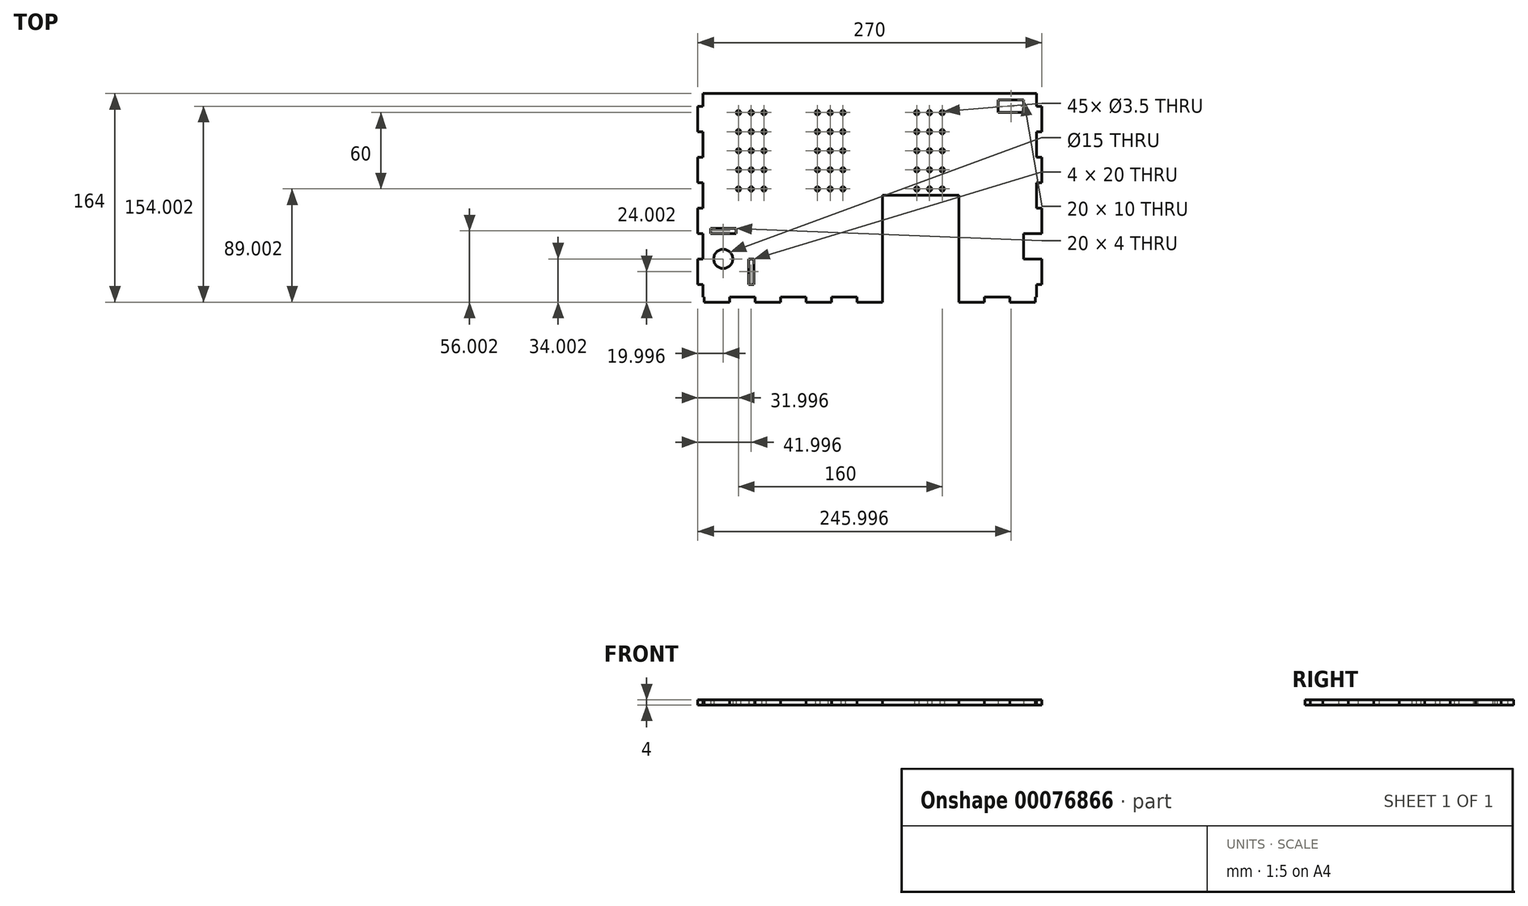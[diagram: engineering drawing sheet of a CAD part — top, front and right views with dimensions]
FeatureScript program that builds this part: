
annotation { "Feature Type Name" : "Feature", "Feature Type Description" : "" }
export const myFeature = defineFeature(function(context is Context, id is Id, definition is map)
    precondition{}
    {
        {
            var Q0;
            Q0=qCreatedBy(makeId("Top.planeOp"),FACE);
            var sketch = newSketch(context, id + "F0", { "sketchPlane" : qUnion([Q0])});
            skLineSegment(sketch, "E0.bottom", {"start": v(-142.44, 35.87) * mm, "end": v(119.56, 35.87) * mm, "construction": true});
            skLineSegment(sketch, "E0.top", {"start": v(-142.44, -124.13) * mm, "end": v(118.25, -124.13) * mm, "construction": true});
            skLineSegment(sketch, "E0.left", {"start": v(-142.44, 35.87) * mm, "end": v(-142.44, -124.13) * mm, "construction": true});
            skLineSegment(sketch, "E1", {"start": v(-11.44, 145.86) * mm, "end": v(-11.44, -140.18) * mm, "construction": true});
            skLineSegment(sketch, "E2.top", {"start": v(-1.44, -128.13) * mm, "end": v(-21.44, -128.13) * mm});
            skLineSegment(sketch, "E2.left", {"start": v(-1.44, -124.13) * mm, "end": v(-1.44, -128.13) * mm});
            skLineSegment(sketch, "E2.right", {"start": v(-21.44, -124.13) * mm, "end": v(-21.44, -128.13) * mm});
            skLineSegment(sketch, "E3.2.0.0", {"start": v(58.56, -124.13) * mm, "end": v(58.56, -128.13) * mm});
            skLineSegment(sketch, "E3.2.0.1", {"start": v(78.56, -128.13) * mm, "end": v(58.56, -128.13) * mm});
            skLineSegment(sketch, "E3.2.0.2", {"start": v(78.56, -124.13) * mm, "end": v(78.56, -128.13) * mm});
            skLineSegment(sketch, "E3.3.0.0", {"start": v(98.56, -124.13) * mm, "end": v(98.56, -128.13) * mm});
            skLineSegment(sketch, "E3.3.0.1", {"start": v(118.56, -128.13) * mm, "end": v(98.56, -128.13) * mm});
            skLineSegment(sketch, "E3.3.0.2", {"start": v(118.56, -124.13) * mm, "end": v(118.56, -128.13) * mm});
            skLineSegment(sketch, "E3.direction1", {"start": v(-21.44, -128.13) * mm, "end": v(18.56, -128.13) * mm, "construction": true});
            skLineSegment(sketch, "E4.1.0.0", {"start": v(-61.44, -124.13) * mm, "end": v(-61.44, -128.13) * mm});
            skLineSegment(sketch, "E4.1.0.1", {"start": v(-41.44, -128.13) * mm, "end": v(-61.44, -128.13) * mm});
            skLineSegment(sketch, "E4.1.0.2", {"start": v(-41.44, -124.13) * mm, "end": v(-41.44, -128.13) * mm});
            skLineSegment(sketch, "E4.2.0.0", {"start": v(-101.44, -124.13) * mm, "end": v(-101.44, -128.13) * mm});
            skLineSegment(sketch, "E4.2.0.1", {"start": v(-81.44, -128.13) * mm, "end": v(-101.44, -128.13) * mm});
            skLineSegment(sketch, "E4.2.0.2", {"start": v(-81.44, -124.13) * mm, "end": v(-81.44, -128.13) * mm});
            skLineSegment(sketch, "E4.direction1", {"start": v(-21.44, -128.13) * mm, "end": v(-61.44, -128.13) * mm, "construction": true});
            skLineSegment(sketch, "E5", {"start": v(78.56, -124.13) * mm, "end": v(98.56, -124.13) * mm});
            skLineSegment(sketch, "E6", {"start": v(-21.44, -124.13) * mm, "end": v(-41.44, -124.13) * mm});
            skLineSegment(sketch, "E7.0.3.0", {"start": v(-141.44, -124.13) * mm, "end": v(-141.44, -128.13) * mm});
            skLineSegment(sketch, "E7.3.3.0", {"start": v(-121.44, -128.13) * mm, "end": v(-141.44, -128.13) * mm});
            skLineSegment(sketch, "E7.6.3.0", {"start": v(-121.44, -124.13) * mm, "end": v(-121.44, -128.13) * mm});
            skLineSegment(sketch, "E8", {"start": v(-61.44, -124.13) * mm, "end": v(-81.44, -124.13) * mm});
            skLineSegment(sketch, "E9", {"start": v(-101.44, -124.13) * mm, "end": v(-121.44, -124.13) * mm});
            skLineSegment(sketch, "E10.top", {"start": v(58.56, -44.13) * mm, "end": v(-1.44, -44.13) * mm});
            skLineSegment(sketch, "E10.left", {"start": v(58.56, -124.13) * mm, "end": v(58.56, -44.13) * mm});
            skLineSegment(sketch, "E10.right", {"start": v(-1.44, -124.13) * mm, "end": v(-1.44, -44.13) * mm});
            skLineSegment(sketch, "E11.bottom", {"start": v(-142.44, -114.13) * mm, "end": v(-146.44, -114.13) * mm});
            skLineSegment(sketch, "E11.top", {"start": v(-142.44, -94.13) * mm, "end": v(-146.44, -94.13) * mm});
            skLineSegment(sketch, "E11.right", {"start": v(-146.44, -114.13) * mm, "end": v(-146.44, -94.13) * mm});
            skLineSegment(sketch, "E12", {"start": v(-142.44, -124.13) * mm, "end": v(-142.44, -114.13) * mm});
            skLineSegment(sketch, "E13.0.1.0", {"start": v(-142.44, -54.13) * mm, "end": v(-146.44, -54.13) * mm});
            skLineSegment(sketch, "E13.0.1.1", {"start": v(-146.44, -74.13) * mm, "end": v(-146.44, -54.13) * mm});
            skLineSegment(sketch, "E13.0.1.2", {"start": v(-142.44, -74.13) * mm, "end": v(-146.44, -74.13) * mm});
            skLineSegment(sketch, "E13.0.2.0", {"start": v(-142.44, -14.13) * mm, "end": v(-146.44, -14.13) * mm});
            skLineSegment(sketch, "E13.0.2.1", {"start": v(-146.44, -34.13) * mm, "end": v(-146.44, -14.13) * mm});
            skLineSegment(sketch, "E13.0.2.2", {"start": v(-142.44, -34.13) * mm, "end": v(-146.44, -34.13) * mm});
            skLineSegment(sketch, "E13.0.3.0", {"start": v(-142.44, 25.87) * mm, "end": v(-146.44, 25.87) * mm});
            skLineSegment(sketch, "E13.0.3.1", {"start": v(-146.44, 5.87) * mm, "end": v(-146.44, 25.87) * mm});
            skLineSegment(sketch, "E13.0.3.2", {"start": v(-142.44, 5.87) * mm, "end": v(-146.44, 5.87) * mm});
            skLineSegment(sketch, "E13.direction1", {"start": v(-146.44, -94.13) * mm, "end": v(-120.62, -94.13) * mm, "construction": true});
            skLineSegment(sketch, "E13.direction2", {"start": v(-146.44, -94.13) * mm, "end": v(-146.44, -54.13) * mm, "construction": true});
            skLineSegment(sketch, "E14", {"start": v(-142.44, -94.13) * mm, "end": v(-142.44, -74.13) * mm});
            skLineSegment(sketch, "E15", {"start": v(-142.44, -54.13) * mm, "end": v(-142.44, -34.13) * mm});
            skLineSegment(sketch, "E16", {"start": v(-142.44, -14.13) * mm, "end": v(-142.44, 5.87) * mm});
            skLineSegment(sketch, "E17", {"start": v(-142.44, 25.87) * mm, "end": v(-142.44, 35.87) * mm});
            skLineSegment(sketch, "E18", {"start": v(-142.44, 35.87) * mm, "end": v(119.56, 35.87) * mm});
            skLineSegment(sketch, "E19.MirrorCS", {"start": v(119.56, -94.13) * mm, "end": v(123.56, -94.13) * mm});
            skLineSegment(sketch, "E20.MirrorCS", {"start": v(119.56, -54.13) * mm, "end": v(123.56, -54.13) * mm});
            skLineSegment(sketch, "E21.MirrorCS", {"start": v(119.56, -34.13) * mm, "end": v(123.56, -34.13) * mm});
            skLineSegment(sketch, "E22.MirrorCS", {"start": v(119.56, 25.87) * mm, "end": v(119.56, 35.87) * mm});
            skLineSegment(sketch, "E23.MirrorCS", {"start": v(119.56, -74.13) * mm, "end": v(123.56, -74.13) * mm});
            skLineSegment(sketch, "E24.MirrorCS", {"start": v(119.56, -14.13) * mm, "end": v(123.56, -14.13) * mm});
            skLineSegment(sketch, "E25.MirrorCS", {"start": v(119.56, 25.87) * mm, "end": v(123.56, 25.87) * mm});
            skLineSegment(sketch, "E26.MirrorCS", {"start": v(119.56, 5.87) * mm, "end": v(123.56, 5.87) * mm});
            skLineSegment(sketch, "E27.MirrorCS", {"start": v(119.56, -114.13) * mm, "end": v(123.56, -114.13) * mm});
            skLineSegment(sketch, "E28.MirrorCS", {"start": v(123.56, 5.87) * mm, "end": v(123.56, 25.87) * mm});
            skLineSegment(sketch, "E29.MirrorCS", {"start": v(119.56, -124.13) * mm, "end": v(119.56, -114.13) * mm});
            skLineSegment(sketch, "E30.MirrorCS", {"start": v(123.56, -74.13) * mm, "end": v(123.56, -54.13) * mm});
            skLineSegment(sketch, "E31.MirrorCS", {"start": v(119.56, -14.13) * mm, "end": v(119.56, 5.87) * mm});
            skLineSegment(sketch, "E32.MirrorCS", {"start": v(123.56, -114.13) * mm, "end": v(123.56, -94.13) * mm});
            skLineSegment(sketch, "E33.MirrorCS", {"start": v(123.56, -94.13) * mm, "end": v(123.56, -54.13) * mm, "construction": true});
            skLineSegment(sketch, "E34.MirrorCS", {"start": v(119.56, 35.87) * mm, "end": v(119.56, -124.13) * mm, "construction": true});
            skLineSegment(sketch, "E35.MirrorCS", {"start": v(119.56, -54.13) * mm, "end": v(119.56, -34.13) * mm});
            skLineSegment(sketch, "E36.MirrorCS", {"start": v(123.56, -34.13) * mm, "end": v(123.56, -14.13) * mm});
            skLineSegment(sketch, "E37", {"start": v(-142.44, -124.13) * mm, "end": v(-141.44, -124.13) * mm});
            skLineSegment(sketch, "E38", {"start": v(118.56, -124.13) * mm, "end": v(119.56, -124.13) * mm});
            skLineSegment(sketch, "E39", {"start": v(-106.44, -68.04) * mm, "end": v(-106.44, -130.18) * mm, "construction": true});
            skLineSegment(sketch, "E40.bottom", {"start": v(-106.44, -94.13) * mm, "end": v(-102.44, -94.13) * mm});
            skLineSegment(sketch, "E40.top", {"start": v(-106.44, -114.13) * mm, "end": v(-102.44, -114.13) * mm});
            skLineSegment(sketch, "E40.left", {"start": v(-106.44, -94.13) * mm, "end": v(-106.44, -114.13) * mm});
            skLineSegment(sketch, "E40.right", {"start": v(-102.44, -94.13) * mm, "end": v(-102.44, -114.13) * mm});
            skLineSegment(sketch, "E41", {"start": v(-142.44, -74.13) * mm, "end": v(-106.44, -74.13) * mm, "construction": true});
            skLineSegment(sketch, "E42.bottom", {"start": v(-136.44, -74.13) * mm, "end": v(-116.44, -74.13) * mm});
            skLineSegment(sketch, "E42.top", {"start": v(-136.44, -70.13) * mm, "end": v(-116.44, -70.13) * mm});
            skLineSegment(sketch, "E42.left", {"start": v(-136.44, -74.13) * mm, "end": v(-136.44, -70.13) * mm});
            skLineSegment(sketch, "E42.right", {"start": v(-116.44, -74.13) * mm, "end": v(-116.44, -70.13) * mm});
            skCircle(sketch, "E43", {"center": v(-126.44, -94.13) * mm, "radius": 7.5 * mm});
            skLineSegment(sketch, "E44.bottom", {"start": v(119.56, -94.13) * mm, "end": v(109.56, -94.13) * mm});
            skLineSegment(sketch, "E44.top", {"start": v(119.56, -74.13) * mm, "end": v(109.56, -74.13) * mm});
            skLineSegment(sketch, "E44.right", {"start": v(109.56, -94.13) * mm, "end": v(109.56, -74.13) * mm});
            skLineSegment(sketch, "E45.bottom", {"start": v(89.56, 30.87) * mm, "end": v(109.56, 30.87) * mm});
            skLineSegment(sketch, "E45.top", {"start": v(89.56, 20.87) * mm, "end": v(109.56, 20.87) * mm});
            skLineSegment(sketch, "E45.left", {"start": v(89.56, 30.87) * mm, "end": v(89.56, 20.87) * mm});
            skLineSegment(sketch, "E45.right", {"start": v(109.56, 30.87) * mm, "end": v(109.56, 20.87) * mm});
            skPoint(sketch, "E46", {"position": v(-127.44, -39.13) * mm});
            skLineSegment(sketch, "E47", {"start": v(-127.44, -39.13) * mm, "end": v(94.24, -39.13) * mm, "construction": true});
            skPoint(sketch, "E48", {"position": v(-104.44, -39.13) * mm});
            skPoint(sketch, "E49", {"position": v(-42.44, -39.13) * mm});
            skPoint(sketch, "E50", {"position": v(35.56, -39.13) * mm});
            skPoint(sketch, "E51", {"position": v(105.56, -39.13) * mm});
            skCircle(sketch, "E52", {"center": v(-104.44, -39.13) * mm, "radius": 1.75 * mm});
            skCircle(sketch, "E53", {"center": v(-42.44, -39.13) * mm, "radius": 1.75 * mm});
            skCircle(sketch, "E54", {"center": v(35.56, -39.13) * mm, "radius": 1.75 * mm});
            skPoint(sketch, "E55", {"position": v(-117.44, -39.13) * mm});
            skLineSegment(sketch, "E56", {"start": v(-117.44, -39.13) * mm, "end": v(104.24, -39.13) * mm, "construction": true});
            skPoint(sketch, "E57", {"position": v(-94.44, -39.13) * mm});
            skPoint(sketch, "E58", {"position": v(-32.44, -39.13) * mm});
            skPoint(sketch, "E59", {"position": v(45.56, -39.13) * mm});
            skPoint(sketch, "E60", {"position": v(115.56, -39.13) * mm});
            skCircle(sketch, "E61", {"center": v(-94.44, -39.13) * mm, "radius": 1.75 * mm});
            skCircle(sketch, "E62", {"center": v(-32.44, -39.13) * mm, "radius": 1.75 * mm});
            skCircle(sketch, "E63", {"center": v(45.56, -39.13) * mm, "radius": 1.75 * mm});
            skPoint(sketch, "E64", {"position": v(-137.44, -39.13) * mm});
            skLineSegment(sketch, "E65", {"start": v(-137.44, -39.13) * mm, "end": v(84.24, -39.13) * mm, "construction": true});
            skPoint(sketch, "E66", {"position": v(-114.44, -39.13) * mm});
            skPoint(sketch, "E67", {"position": v(-52.44, -39.13) * mm});
            skPoint(sketch, "E68", {"position": v(25.56, -39.13) * mm});
            skPoint(sketch, "E69", {"position": v(95.56, -39.13) * mm});
            skCircle(sketch, "E70", {"center": v(-114.44, -39.13) * mm, "radius": 1.75 * mm});
            skCircle(sketch, "E71", {"center": v(-52.44, -39.13) * mm, "radius": 1.75 * mm});
            skCircle(sketch, "E72", {"center": v(25.56, -39.13) * mm, "radius": 1.75 * mm});
            skPoint(sketch, "E73.0.1.0", {"position": v(95.56, -24.13) * mm});
            skLineSegment(sketch, "E73.0.1.1", {"start": v(-127.44, -24.13) * mm, "end": v(94.24, -24.13) * mm, "construction": true});
            skPoint(sketch, "E73.0.1.2", {"position": v(35.56, -24.13) * mm});
            skPoint(sketch, "E73.0.1.3", {"position": v(25.56, -24.13) * mm});
            skPoint(sketch, "E73.0.1.4", {"position": v(105.56, -24.13) * mm});
            skPoint(sketch, "E73.0.1.5", {"position": v(-127.44, -24.13) * mm});
            skLineSegment(sketch, "E73.0.1.6", {"start": v(-11.44, 160.86) * mm, "end": v(-11.44, -125.18) * mm, "construction": true});
            skPoint(sketch, "E73.0.1.7", {"position": v(-137.44, -24.13) * mm});
            skPoint(sketch, "E73.0.1.8", {"position": v(45.56, -24.13) * mm});
            skPoint(sketch, "E73.0.1.9", {"position": v(-52.44, -24.13) * mm});
            skPoint(sketch, "E73.0.1.10", {"position": v(-42.44, -24.13) * mm});
            skPoint(sketch, "E73.0.1.11", {"position": v(-32.44, -24.13) * mm});
            skPoint(sketch, "E73.0.1.12", {"position": v(115.56, -24.13) * mm});
            skLineSegment(sketch, "E73.0.1.13", {"start": v(-117.44, -24.13) * mm, "end": v(104.24, -24.13) * mm, "construction": true});
            skLineSegment(sketch, "E73.0.1.14", {"start": v(-137.44, -24.13) * mm, "end": v(84.24, -24.13) * mm, "construction": true});
            skPoint(sketch, "E73.0.1.15", {"position": v(-117.44, -24.13) * mm});
            skPoint(sketch, "E73.0.1.16", {"position": v(-94.44, -24.13) * mm});
            skPoint(sketch, "E73.0.1.17", {"position": v(-114.44, -24.13) * mm});
            skPoint(sketch, "E73.0.1.18", {"position": v(-104.44, -24.13) * mm});
            skCircle(sketch, "E73.0.1.19", {"center": v(-42.44, -24.13) * mm, "radius": 1.75 * mm});
            skCircle(sketch, "E73.0.1.20", {"center": v(25.56, -24.13) * mm, "radius": 1.75 * mm});
            skCircle(sketch, "E73.0.1.21", {"center": v(-32.44, -24.13) * mm, "radius": 1.75 * mm});
            skCircle(sketch, "E73.0.1.22", {"center": v(-52.44, -24.13) * mm, "radius": 1.75 * mm});
            skCircle(sketch, "E73.0.1.23", {"center": v(35.56, -24.13) * mm, "radius": 1.75 * mm});
            skCircle(sketch, "E73.0.1.24", {"center": v(45.56, -24.13) * mm, "radius": 1.75 * mm});
            skCircle(sketch, "E73.0.1.25", {"center": v(-94.44, -24.13) * mm, "radius": 1.75 * mm});
            skCircle(sketch, "E73.0.1.26", {"center": v(-114.44, -24.13) * mm, "radius": 1.75 * mm});
            skCircle(sketch, "E73.0.1.27", {"center": v(-104.44, -24.13) * mm, "radius": 1.75 * mm});
            skPoint(sketch, "E73.0.2.0", {"position": v(95.56, -9.13) * mm});
            skLineSegment(sketch, "E73.0.2.1", {"start": v(-127.44, -9.13) * mm, "end": v(94.24, -9.13) * mm, "construction": true});
            skPoint(sketch, "E73.0.2.2", {"position": v(35.56, -9.13) * mm});
            skPoint(sketch, "E73.0.2.3", {"position": v(25.56, -9.13) * mm});
            skPoint(sketch, "E73.0.2.4", {"position": v(105.56, -9.13) * mm});
            skPoint(sketch, "E73.0.2.5", {"position": v(-127.44, -9.13) * mm});
            skLineSegment(sketch, "E73.0.2.6", {"start": v(-11.44, 175.86) * mm, "end": v(-11.44, -110.18) * mm, "construction": true});
            skPoint(sketch, "E73.0.2.7", {"position": v(-137.44, -9.13) * mm});
            skPoint(sketch, "E73.0.2.8", {"position": v(45.56, -9.13) * mm});
            skPoint(sketch, "E73.0.2.9", {"position": v(-52.44, -9.13) * mm});
            skPoint(sketch, "E73.0.2.10", {"position": v(-42.44, -9.13) * mm});
            skPoint(sketch, "E73.0.2.11", {"position": v(-32.44, -9.13) * mm});
            skPoint(sketch, "E73.0.2.12", {"position": v(115.56, -9.13) * mm});
            skLineSegment(sketch, "E73.0.2.13", {"start": v(-117.44, -9.13) * mm, "end": v(104.24, -9.13) * mm, "construction": true});
            skLineSegment(sketch, "E73.0.2.14", {"start": v(-137.44, -9.13) * mm, "end": v(84.24, -9.13) * mm, "construction": true});
            skPoint(sketch, "E73.0.2.15", {"position": v(-117.44, -9.13) * mm});
            skPoint(sketch, "E73.0.2.16", {"position": v(-94.44, -9.13) * mm});
            skPoint(sketch, "E73.0.2.17", {"position": v(-114.44, -9.13) * mm});
            skPoint(sketch, "E73.0.2.18", {"position": v(-104.44, -9.13) * mm});
            skCircle(sketch, "E73.0.2.19", {"center": v(-42.44, -9.13) * mm, "radius": 1.75 * mm});
            skCircle(sketch, "E73.0.2.20", {"center": v(25.56, -9.13) * mm, "radius": 1.75 * mm});
            skCircle(sketch, "E73.0.2.21", {"center": v(-32.44, -9.13) * mm, "radius": 1.75 * mm});
            skCircle(sketch, "E73.0.2.22", {"center": v(-52.44, -9.13) * mm, "radius": 1.75 * mm});
            skCircle(sketch, "E73.0.2.23", {"center": v(35.56, -9.13) * mm, "radius": 1.75 * mm});
            skCircle(sketch, "E73.0.2.24", {"center": v(45.56, -9.13) * mm, "radius": 1.75 * mm});
            skCircle(sketch, "E73.0.2.25", {"center": v(-94.44, -9.13) * mm, "radius": 1.75 * mm});
            skCircle(sketch, "E73.0.2.26", {"center": v(-114.44, -9.13) * mm, "radius": 1.75 * mm});
            skCircle(sketch, "E73.0.2.27", {"center": v(-104.44, -9.13) * mm, "radius": 1.75 * mm});
            skPoint(sketch, "E73.0.3.0", {"position": v(95.56, 5.87) * mm});
            skLineSegment(sketch, "E73.0.3.1", {"start": v(-127.44, 5.87) * mm, "end": v(94.24, 5.87) * mm, "construction": true});
            skPoint(sketch, "E73.0.3.2", {"position": v(35.56, 5.87) * mm});
            skPoint(sketch, "E73.0.3.3", {"position": v(25.56, 5.87) * mm});
            skPoint(sketch, "E73.0.3.4", {"position": v(105.56, 5.87) * mm});
            skPoint(sketch, "E73.0.3.5", {"position": v(-127.44, 5.87) * mm});
            skLineSegment(sketch, "E73.0.3.6", {"start": v(-11.44, 190.86) * mm, "end": v(-11.44, -95.18) * mm, "construction": true});
            skPoint(sketch, "E73.0.3.7", {"position": v(-137.44, 5.87) * mm});
            skPoint(sketch, "E73.0.3.8", {"position": v(45.56, 5.87) * mm});
            skPoint(sketch, "E73.0.3.9", {"position": v(-52.44, 5.87) * mm});
            skPoint(sketch, "E73.0.3.10", {"position": v(-42.44, 5.87) * mm});
            skPoint(sketch, "E73.0.3.11", {"position": v(-32.44, 5.87) * mm});
            skPoint(sketch, "E73.0.3.12", {"position": v(115.56, 5.87) * mm});
            skLineSegment(sketch, "E73.0.3.13", {"start": v(-117.44, 5.87) * mm, "end": v(104.24, 5.87) * mm, "construction": true});
            skLineSegment(sketch, "E73.0.3.14", {"start": v(-137.44, 5.87) * mm, "end": v(84.24, 5.87) * mm, "construction": true});
            skPoint(sketch, "E73.0.3.15", {"position": v(-117.44, 5.87) * mm});
            skPoint(sketch, "E73.0.3.16", {"position": v(-94.44, 5.87) * mm});
            skPoint(sketch, "E73.0.3.17", {"position": v(-114.44, 5.87) * mm});
            skPoint(sketch, "E73.0.3.18", {"position": v(-104.44, 5.87) * mm});
            skCircle(sketch, "E73.0.3.19", {"center": v(-42.44, 5.87) * mm, "radius": 1.75 * mm});
            skCircle(sketch, "E73.0.3.20", {"center": v(25.56, 5.87) * mm, "radius": 1.75 * mm});
            skCircle(sketch, "E73.0.3.21", {"center": v(-32.44, 5.87) * mm, "radius": 1.75 * mm});
            skCircle(sketch, "E73.0.3.22", {"center": v(-52.44, 5.87) * mm, "radius": 1.75 * mm});
            skCircle(sketch, "E73.0.3.23", {"center": v(35.56, 5.87) * mm, "radius": 1.75 * mm});
            skCircle(sketch, "E73.0.3.24", {"center": v(45.56, 5.87) * mm, "radius": 1.75 * mm});
            skCircle(sketch, "E73.0.3.25", {"center": v(-94.44, 5.87) * mm, "radius": 1.75 * mm});
            skCircle(sketch, "E73.0.3.26", {"center": v(-114.44, 5.87) * mm, "radius": 1.75 * mm});
            skCircle(sketch, "E73.0.3.27", {"center": v(-104.44, 5.87) * mm, "radius": 1.75 * mm});
            skPoint(sketch, "E73.0.4.0", {"position": v(95.56, 20.87) * mm});
            skLineSegment(sketch, "E73.0.4.1", {"start": v(-127.44, 20.87) * mm, "end": v(94.24, 20.87) * mm, "construction": true});
            skPoint(sketch, "E73.0.4.2", {"position": v(35.56, 20.87) * mm});
            skPoint(sketch, "E73.0.4.3", {"position": v(25.56, 20.87) * mm});
            skPoint(sketch, "E73.0.4.4", {"position": v(105.56, 20.87) * mm});
            skPoint(sketch, "E73.0.4.5", {"position": v(-127.44, 20.87) * mm});
            skLineSegment(sketch, "E73.0.4.6", {"start": v(-11.44, 205.86) * mm, "end": v(-11.44, -80.18) * mm, "construction": true});
            skPoint(sketch, "E73.0.4.7", {"position": v(-137.44, 20.87) * mm});
            skPoint(sketch, "E73.0.4.8", {"position": v(45.56, 20.87) * mm});
            skPoint(sketch, "E73.0.4.9", {"position": v(-52.44, 20.87) * mm});
            skPoint(sketch, "E73.0.4.10", {"position": v(-42.44, 20.87) * mm});
            skPoint(sketch, "E73.0.4.11", {"position": v(-32.44, 20.87) * mm});
            skPoint(sketch, "E73.0.4.12", {"position": v(115.56, 20.87) * mm});
            skLineSegment(sketch, "E73.0.4.13", {"start": v(-117.44, 20.87) * mm, "end": v(104.24, 20.87) * mm, "construction": true});
            skLineSegment(sketch, "E73.0.4.14", {"start": v(-137.44, 20.87) * mm, "end": v(84.24, 20.87) * mm, "construction": true});
            skPoint(sketch, "E73.0.4.15", {"position": v(-117.44, 20.87) * mm});
            skPoint(sketch, "E73.0.4.16", {"position": v(-94.44, 20.87) * mm});
            skPoint(sketch, "E73.0.4.17", {"position": v(-114.44, 20.87) * mm});
            skPoint(sketch, "E73.0.4.18", {"position": v(-104.44, 20.87) * mm});
            skCircle(sketch, "E73.0.4.19", {"center": v(-42.44, 20.87) * mm, "radius": 1.75 * mm});
            skCircle(sketch, "E73.0.4.20", {"center": v(25.56, 20.87) * mm, "radius": 1.75 * mm});
            skCircle(sketch, "E73.0.4.21", {"center": v(-32.44, 20.87) * mm, "radius": 1.75 * mm});
            skCircle(sketch, "E73.0.4.22", {"center": v(-52.44, 20.87) * mm, "radius": 1.75 * mm});
            skCircle(sketch, "E73.0.4.23", {"center": v(35.56, 20.87) * mm, "radius": 1.75 * mm});
            skCircle(sketch, "E73.0.4.24", {"center": v(45.56, 20.87) * mm, "radius": 1.75 * mm});
            skCircle(sketch, "E73.0.4.25", {"center": v(-94.44, 20.87) * mm, "radius": 1.75 * mm});
            skCircle(sketch, "E73.0.4.26", {"center": v(-114.44, 20.87) * mm, "radius": 1.75 * mm});
            skCircle(sketch, "E73.0.4.27", {"center": v(-104.44, 20.87) * mm, "radius": 1.75 * mm});
            skLineSegment(sketch, "E73.direction1", {"start": v(95.56, -39.13) * mm, "end": v(120.56, -39.13) * mm, "construction": true});
            skLineSegment(sketch, "E73.direction2", {"start": v(95.56, -39.13) * mm, "end": v(95.56, -24.13) * mm, "construction": true});
            skSolve(sketch);
        }
        {
            var Q0;
            Q0 = qSketchRegion(id + "F0", true);
            extrude(context, id + "F1", {"entities" : qUnion([Q0]), "depth" : 4 * mm});
        }
    });
